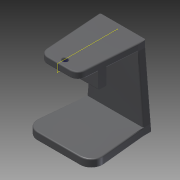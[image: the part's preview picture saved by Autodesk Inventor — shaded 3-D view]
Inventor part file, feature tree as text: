
AUTODESK INVENTOR PART (.ipt)
format: ipt  version: 2016 SP1 (Build 200210100, 210)  size: 267,264 bytes
history: native  units: mm
features: extrude x4, sketch x4, projected_geometry x3, fillet x2, plane x1
ambient origin geometry x8: Origin, YZ Plane, XZ Plane, XY Plane, X Axis, Y Axis, Z Axis, Center Point
bodies: Solid1 (feature_tree)
feature tree (14):
  extrude  "Extrusion1"  Depth=10.0mm
  plane  "Work Plane1"
  extrude  "Extrusion2"  Depth=10.0mm
  extrude  "Extrusion3"  Depth=10.0mm TaperAngle=0.0deg
  extrude  "Extrusion4"  Depth=0.5mm
  fillet  "Fillet2"  Radius=3.5mm
  fillet  "Fillet5"  Radius=30.0mm
  sketch  "Sketch1"  dims[d0=3.0mm d1=0.0mm d3=10.0mm]
  sketch  "Sketch3"  dims[d4=5.0mm d6=10.0mm]
  sketch  "Sketch5"  dims[d7=3.5mm d8=10.0mm d9=0.0mm]
  sketch  "Sketch6"  dims[d10=28.0mm d11=25.0mm d12=3.5mm d13=0.0mm d14=30.0mm d15=15.0mm d16=25.0mm d17=3.5mm d18=0.0mm d19=5.0mm d22=0.5mm]
  projected_geometry  "Project Cut Edges1"
  projected_geometry  "Project Cut Edges2"
  projected_geometry  "Project Cut Edges3"
